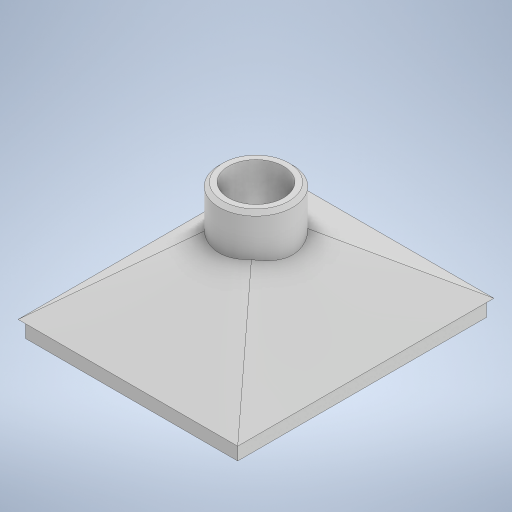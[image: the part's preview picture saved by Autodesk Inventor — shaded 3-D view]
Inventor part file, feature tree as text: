
AUTODESK INVENTOR PART (.ipt)
format: ipt  version: 2023 (Build 270158000, 158)  size: 411,648 bytes
history: native  units: mm
features: sketch x7, extrude x4, chamfer x2, plane x1, loft x1, hole x1, shell x1, fillet x1
ambient origin geometry x8: Origin, YZ Plane, XZ Plane, XY Plane, X Axis, Y Axis, Z Axis, Center Point
bodies: Solid1 (feature_tree)
feature tree (18):
  sketch  "Sketch1"  dims[d0=60.0mm d1=70.0mm]
  plane  "Work Plane1"
  loft  "Loft1"
  hole  "Hole1"  [1 undecoded]
  sketch  "Sketch10"  dims[d9=15.0mm d10=6.0mm d11=4.0mm d12=2.0mm d13=90.0deg d14=8.0mm d15=20.594885mm d16=1.0mm]
  shell  "Shell1"  Thickness=0.0mm
  extrude  "Extrusion1"  Depth=1.0mm
  extrude  "Extrusion2"  Depth=1.0mm
  fillet  "Fillet2"  Radius=1.0mm
  chamfer  "Chamfer1"  Distance=5.0mm
  extrude  "Extrusion3"  Depth=10.0mm
  extrude  "Extrusion4"  Depth=10.0mm
  chamfer  "Chamfer2"  Distance=1.0mm
  sketch  "Sketch2"  dims[d2=20.0mm d3=15.0mm d4=0.0mm d5=90.0deg]
  sketch  "Sketch6"  dims[d6=0.0mm d7=90.0deg]
  sketch  "Sketch12"  dims[d20=1.0mm d21=1.0mm d22=1.0mm]
  sketch  "Sketch13"  dims[d23=1.0mm d24=5.0mm d25=0.0mm]
  sketch  "Sketch14"  dims[d26=1.0mm d27=1.0mm d28=1.0mm d29=1.0mm d30=5.0mm d31=0.0mm d32=10.0mm d33=0.5mm d34=2.0mm d35=45.0deg d36=20.0mm d37=5.0mm d38=0.0mm d39=10.0mm d40=0.0mm d41=1.0mm d42=2.0mm d43=45.0deg]
note: 1 required parameter value undecoded (feature->parameter linkage not recoverable at this tier; creation-order binding heuristic only, values carry confidence <= 0.55)
